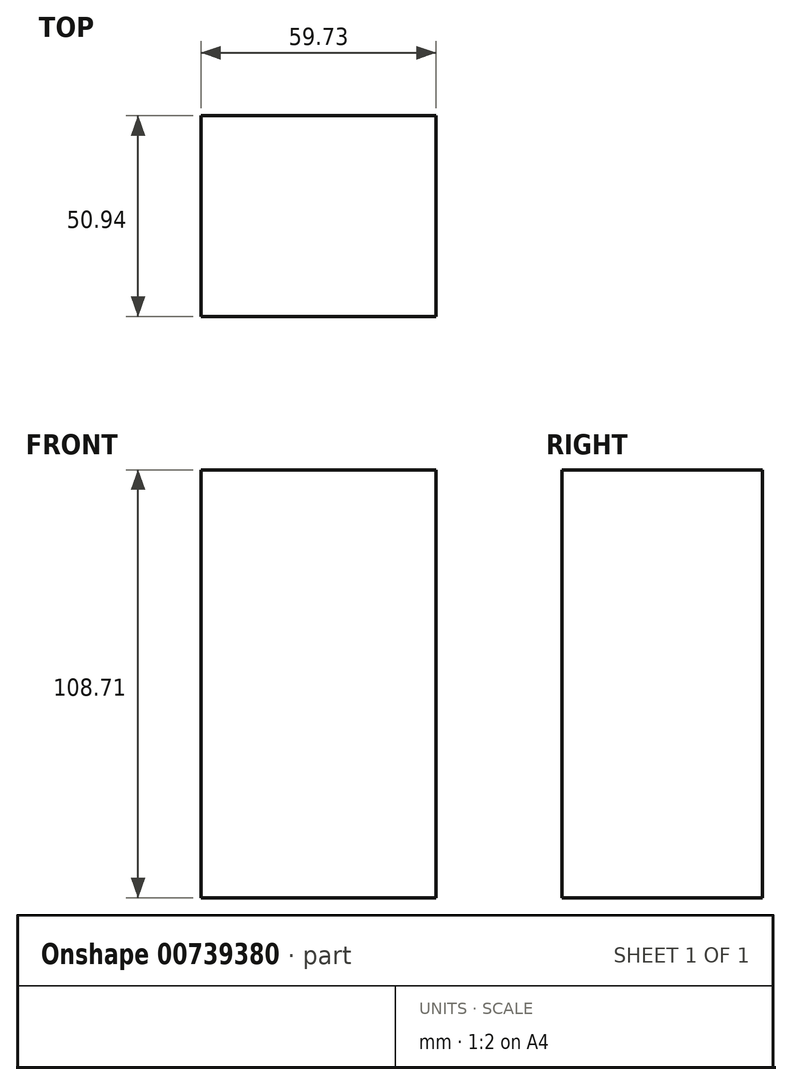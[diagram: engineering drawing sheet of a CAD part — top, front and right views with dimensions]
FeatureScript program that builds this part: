
annotation { "Feature Type Name" : "Feature", "Feature Type Description" : "" }
export const myFeature = defineFeature(function(context is Context, id is Id, definition is map)
    precondition{}
    {
        {
            var Q0;
            Q0=qCreatedBy(makeId("Top.planeOp"),FACE);
            var sketch = newSketch(context, id + "F0", { "sketchPlane" : qUnion([Q0])});
            skLineSegment(sketch, "E0.bottom", {"start": v(-20.84, 61.42) * mm, "end": v(38.89, 61.42) * mm});
            skLineSegment(sketch, "E0.top", {"start": v(-20.84, 10.48) * mm, "end": v(38.89, 10.48) * mm});
            skLineSegment(sketch, "E0.left", {"start": v(-20.84, 61.42) * mm, "end": v(-20.84, 10.48) * mm});
            skLineSegment(sketch, "E0.right", {"start": v(38.89, 61.42) * mm, "end": v(38.89, 10.48) * mm});
            skSolve(sketch);
        }
        {
            var Q0;
            Q0 = qSketchRegion(id + "F0", true);
            extrude(context, id + "F1", {"entities" : qUnion([Q0]), "depth" : 108.7 * mm, "offsetDistance" : 25.4 * mm});
        }
    });
